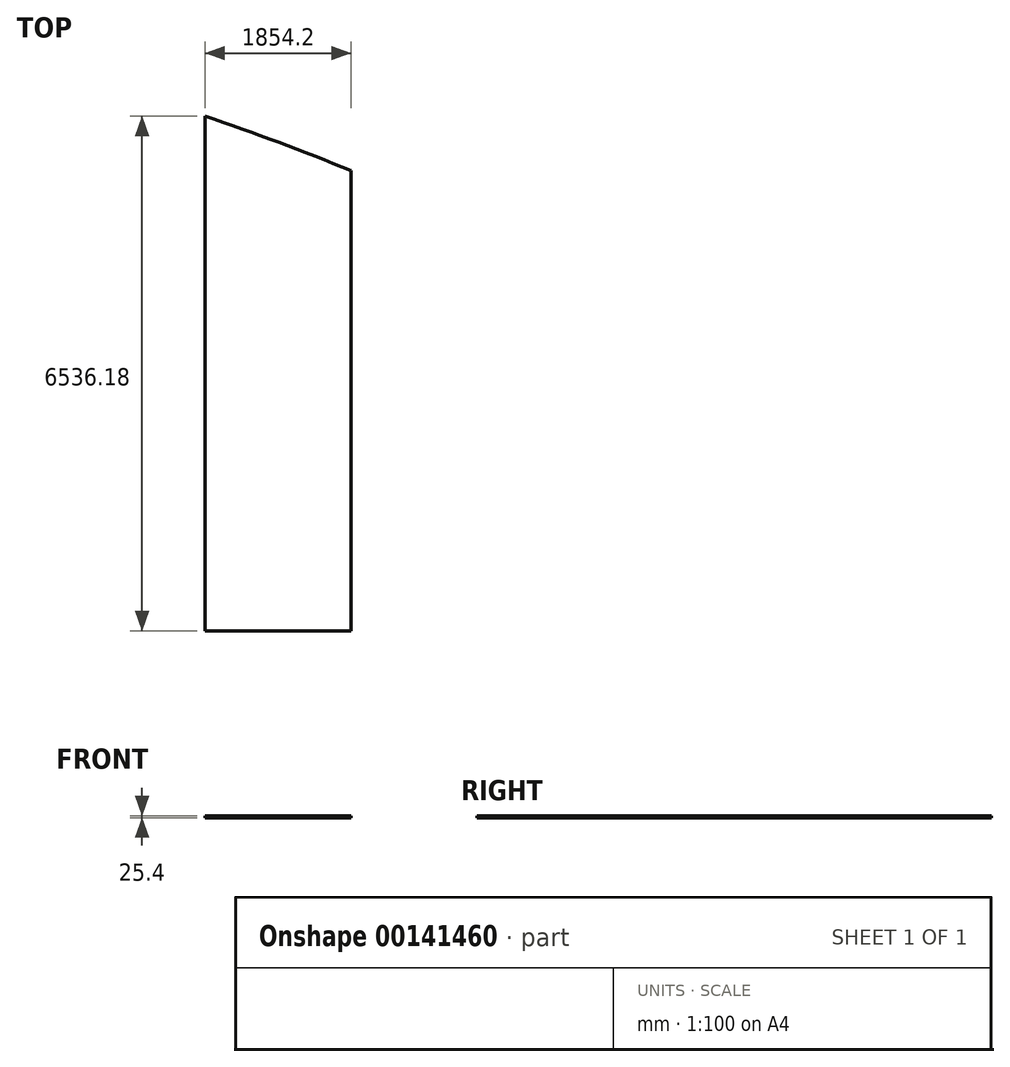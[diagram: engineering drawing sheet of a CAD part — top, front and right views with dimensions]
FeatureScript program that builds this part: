
annotation { "Feature Type Name" : "Feature", "Feature Type Description" : "" }
export const myFeature = defineFeature(function(context is Context, id is Id, definition is map)
    precondition{}
    {
        {
            var Q0;
            Q0=qCreatedBy(makeId("Top.planeOp"),FACE);
            var sketch = newSketch(context, id + "F0", { "sketchPlane" : qUnion([Q0])});
            skLineSegment(sketch, "E0", {"start": v(-948.99, -2417.57) * mm, "end": v(905.21, -2417.57) * mm});
            skLineSegment(sketch, "E1", {"start": v(-948.99, -2417.57) * mm, "end": v(-948.99, 4118.6) * mm});
            skLineSegment(sketch, "E2", {"start": v(905.21, -2417.57) * mm, "end": v(905.21, 3426.97) * mm});
            skLineSegment(sketch, "E3", {"start": v(-21.89, -2417.57) * mm, "end": v(-21.89, 3788.4) * mm});
            skArc(sketch, "E4", {"start": v(905.21, 3426.97) * mm, "mid": v(-16.77, 3786.5) * mm, "end": v(-948.99, 4118.6) * mm});
            skSolve(sketch);
        }
        {
            var Q0;
            {var subQ0=sQuery(id+"F0.wireOp",EDGE,"E1");Q0=makeQuery(id+"F0.imprint","IMPRINT",FACE,{"disambiguationData":[TD([[makeQuery(id+"F0.imprint","IMPRINT",EDGE,{"derivedFrom":subQ0}),-1.0]])]});}
            var Q1;
            {var subQ0=sQuery(id+"F0.wireOp",EDGE,"E2");Q1=makeQuery(id+"F0.imprint","IMPRINT",FACE,{"disambiguationData":[TD([[makeQuery(id+"F0.imprint","IMPRINT",EDGE,{"derivedFrom":subQ0}),1.0]])]});}
            extrude(context, id + "F1", {"entities" : qUnion([Q0, Q1]), "depth" : 25.4 * mm});
        }
    });
